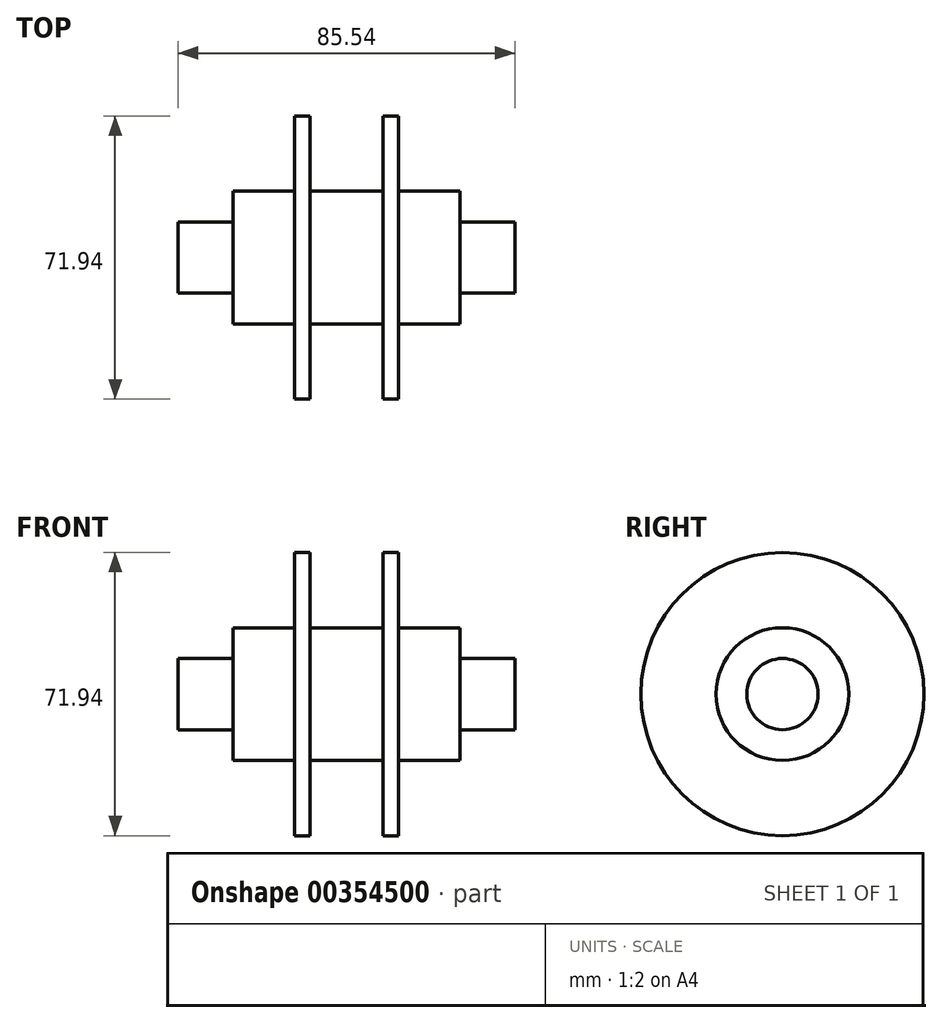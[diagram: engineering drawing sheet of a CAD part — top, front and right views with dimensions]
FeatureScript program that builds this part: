
annotation { "Feature Type Name" : "Feature", "Feature Type Description" : "" }
export const myFeature = defineFeature(function(context is Context, id is Id, definition is map)
    precondition{}
    {
        {
            var Q0;
            Q0=qCreatedBy(makeId("Front.planeOp"),FACE);
            var sketch = newSketch(context, id + "F0", { "sketchPlane" : qUnion([Q0])});
            skLineSegment(sketch, "E0", {"start": v(-13.23, 35.97) * mm, "end": v(-13.23, 16.87) * mm});
            skLineSegment(sketch, "E1", {"start": v(-13.23, 16.87) * mm, "end": v(-28.85, 16.87) * mm});
            skLineSegment(sketch, "E2", {"start": v(-28.85, 16.87) * mm, "end": v(-28.85, 9.04) * mm});
            skLineSegment(sketch, "E3", {"start": v(-28.85, 9.04) * mm, "end": v(-42.77, 9.04) * mm});
            skLineSegment(sketch, "E4", {"start": v(-42.77, 9.04) * mm, "end": v(-42.77, 0) * mm});
            skLineSegment(sketch, "E5", {"start": v(-42.77, 0) * mm, "end": v(0, 0) * mm});
            skLineSegment(sketch, "E6", {"start": v(0, 0) * mm, "end": v(0, 16.87) * mm});
            skLineSegment(sketch, "E7", {"start": v(0, 16.87) * mm, "end": v(-9.32, 16.87) * mm});
            skLineSegment(sketch, "E8", {"start": v(-9.32, 16.87) * mm, "end": v(-9.32, 35.97) * mm});
            skLineSegment(sketch, "E9", {"start": v(-9.32, 35.97) * mm, "end": v(-13.23, 35.97) * mm});
            skSolve(sketch);
        }
        {
            var Q0;
            Q0=makeQuery(id+"F0.imprint","IMPRINT",FACE,{"disambiguationData":[TD([[makeQuery(id+"F0.imprint","IMPRINT",EDGE,{"derivedFrom":sQuery(id+"F0.wireOp",EDGE,"E0")}),1.0]])]});
            var Q1;
            Q1=sQuery(id+"F0.wireOp",EDGE,"E5");
            revolve(context, id + "F1", {"entities" : qUnion([Q0]), "axis" : qUnion([Q1]), "revolveType" : RevolveType.FULL});
        }
        {
            var Q0;
            Q0 = qSketchRegion(id + "F0", true);
            var Q1;
            Q1=makeQuery(id+"F1.opRevolve","SWEPT_FACE",FACE,{"disambiguationData":[OSD([sQuery(id+"F0.wireOp",EDGE,"E7")])]});
            revolve(context, id + "F2", {"operationType" : NewBodyOperationType.ADD, "entities" : qUnion([Q0]), "axis" : qUnion([Q1]), "revolveType" : RevolveType.FULL});
        }
        {
            var Q0;
            Q0=makeQuery(id+"F1.opRevolve","SWEPT_BODY",BODY,{"disambiguationData":[OSD([sQuery(id+"F0.wireOp",EDGE,"E0"),sQuery(id+"F0.wireOp",EDGE,"E1"),sQuery(id+"F0.wireOp",EDGE,"E2"),sQuery(id+"F0.wireOp",EDGE,"E3"),sQuery(id+"F0.wireOp",EDGE,"E4"),sQuery(id+"F0.wireOp",EDGE,"E5"),sQuery(id+"F0.wireOp",EDGE,"E6"),sQuery(id+"F0.wireOp",EDGE,"E7"),sQuery(id+"F0.wireOp",EDGE,"E8"),sQuery(id+"F0.wireOp",EDGE,"E9")])]});
            var Q1;
            Q1=qCreatedBy(makeId("Right.planeOp"),FACE);
            mirror(context, id + "F3", {"operationType" : NewBodyOperationType.ADD, "entities" : qUnion([Q0]), "mirrorPlane" : qUnion([Q1])});
        }
    });
